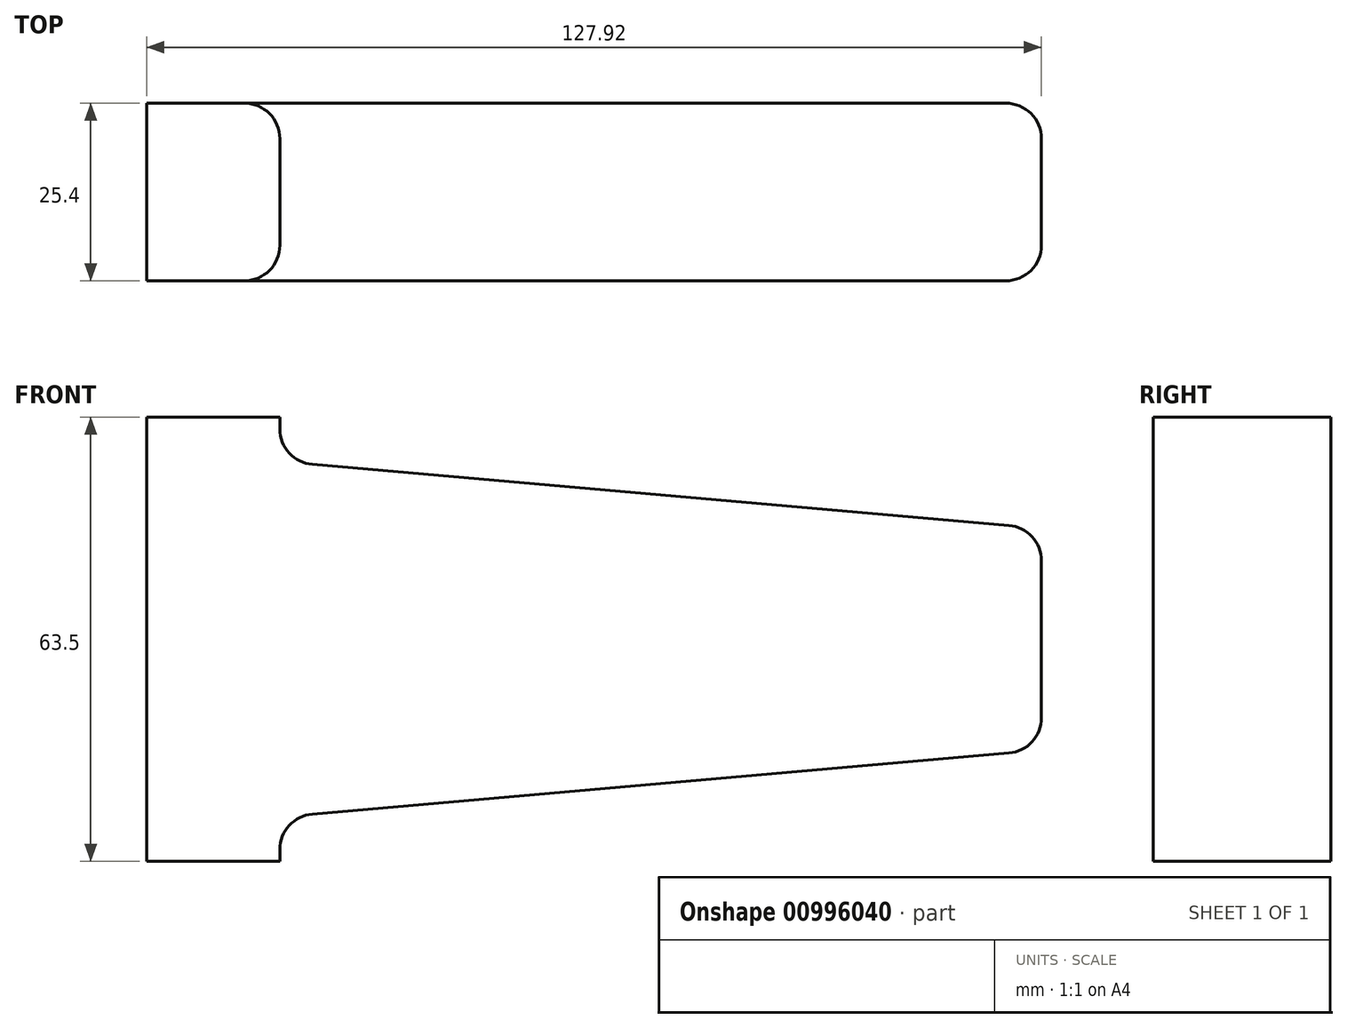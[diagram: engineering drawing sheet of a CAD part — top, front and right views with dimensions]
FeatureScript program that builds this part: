
annotation { "Feature Type Name" : "Feature", "Feature Type Description" : "" }
export const myFeature = defineFeature(function(context is Context, id is Id, definition is map)
    precondition{}
    {
        {
            var Q0;
            Q0=qCreatedBy(makeId("Front.planeOp"),FACE);
            var sketch = newSketch(context, id + "F0", { "sketchPlane" : qUnion([Q0])});
            skLineSegment(sketch, "E0", {"start": v(0, -25.4) * mm, "end": v(0, 25.4) * mm});
            skLineSegment(sketch, "E1", {"start": v(0, 25.4) * mm, "end": v(108.87, 15.88) * mm});
            skLineSegment(sketch, "E2", {"start": v(108.87, 15.88) * mm, "end": v(108.87, -15.87) * mm});
            skLineSegment(sketch, "E3", {"start": v(108.87, -15.87) * mm, "end": v(0, -25.4) * mm});
            skLineSegment(sketch, "E4", {"start": v(0, 25.4) * mm, "end": v(0, 31.75) * mm});
            skLineSegment(sketch, "E5", {"start": v(0, 31.75) * mm, "end": v(-19.05, 31.75) * mm});
            skLineSegment(sketch, "E6", {"start": v(-19.05, 31.75) * mm, "end": v(-19.05, -31.75) * mm});
            skLineSegment(sketch, "E7", {"start": v(-19.05, -31.75) * mm, "end": v(0, -31.75) * mm});
            skLineSegment(sketch, "E8", {"start": v(0, -31.75) * mm, "end": v(0, -25.4) * mm});
            skSolve(sketch);
        }
        {
            var Q0;
            Q0 = qSketchRegion(id + "F0", true);
            extrude(context, id + "F1", {"entities" : qUnion([Q0]), "endBound" : BoundingType.SYMMETRIC, "oppositeDirection" : true, "depth" : 25.4 * mm, "offsetDistance" : 25.4 * mm});
        }
        {
            var Q0;
            Q0=makeQuery(id+"F1.opExtrude","SWEPT_EDGE",EDGE,{"disambiguationData":[OSD([sQuery(id+"F0.wireOp",EDGE,"E0"),sQuery(id+"F0.wireOp",EDGE,"E1"),sQuery(id+"F0.wireOp",EDGE,"E4")])]});
            var Q1;
            Q1=makeQuery(id+"F1.opExtrude","SWEPT_EDGE",EDGE,{"disambiguationData":[OSD([sQuery(id+"F0.wireOp",EDGE,"E0"),sQuery(id+"F0.wireOp",EDGE,"E3"),sQuery(id+"F0.wireOp",EDGE,"E8")])]});
            fillet(context, id + "F2", {"entities" : qUnion([Q0, Q1]), "radius" : 5.08 * mm, "tangentPropagation" : true, "allowEdgeOverflow" : false});
        }
        {
            var Q0;
            Q0=makeQuery(id+"F1.opExtrude","CAP_EDGE",EDGE,{"disambiguationData":[OSD([sQuery(id+"F0.wireOp",EDGE,"E1")])],"isStart":true});
            var Q1;
            Q1=makeQuery(id+"F1.opExtrude","SWEPT_EDGE",EDGE,{"disambiguationData":[OSD([sQuery(id+"F0.wireOp",EDGE,"E1"),sQuery(id+"F0.wireOp",EDGE,"E2")])]});
            var Q2;
            Q2=makeQuery(id+"F1.opExtrude","CAP_EDGE",EDGE,{"disambiguationData":[OSD([sQuery(id+"F0.wireOp",EDGE,"E1")])],"isStart":false});
            var Q3;
            Q3=makeQuery(id+"F1.opExtrude","CAP_EDGE",EDGE,{"disambiguationData":[OSD([sQuery(id+"F0.wireOp",EDGE,"E2")])],"isStart":false});
            var Q4;
            Q4=makeQuery(id+"F1.opExtrude","CAP_EDGE",EDGE,{"disambiguationData":[OSD([sQuery(id+"F0.wireOp",EDGE,"E2")])],"isStart":true});
            var Q5;
            Q5=makeQuery(id+"F1.opExtrude","CAP_EDGE",EDGE,{"disambiguationData":[OSD([sQuery(id+"F0.wireOp",EDGE,"E3")])],"isStart":false});
            var Q6;
            Q6=makeQuery(id+"F1.opExtrude","CAP_EDGE",EDGE,{"disambiguationData":[OSD([sQuery(id+"F0.wireOp",EDGE,"E3")])],"isStart":true});
            var Q7;
            Q7=makeQuery(id+"F1.opExtrude","SWEPT_EDGE",EDGE,{"disambiguationData":[OSD([sQuery(id+"F0.wireOp",EDGE,"E2"),sQuery(id+"F0.wireOp",EDGE,"E3")])]});
            fillet(context, id + "F3", {"entities" : qUnion([Q0, Q1, Q2, Q3, Q4, Q5, Q6, Q7]), "radius" : 5.08 * mm, "tangentPropagation" : true, "allowEdgeOverflow" : false});
        }
    });
